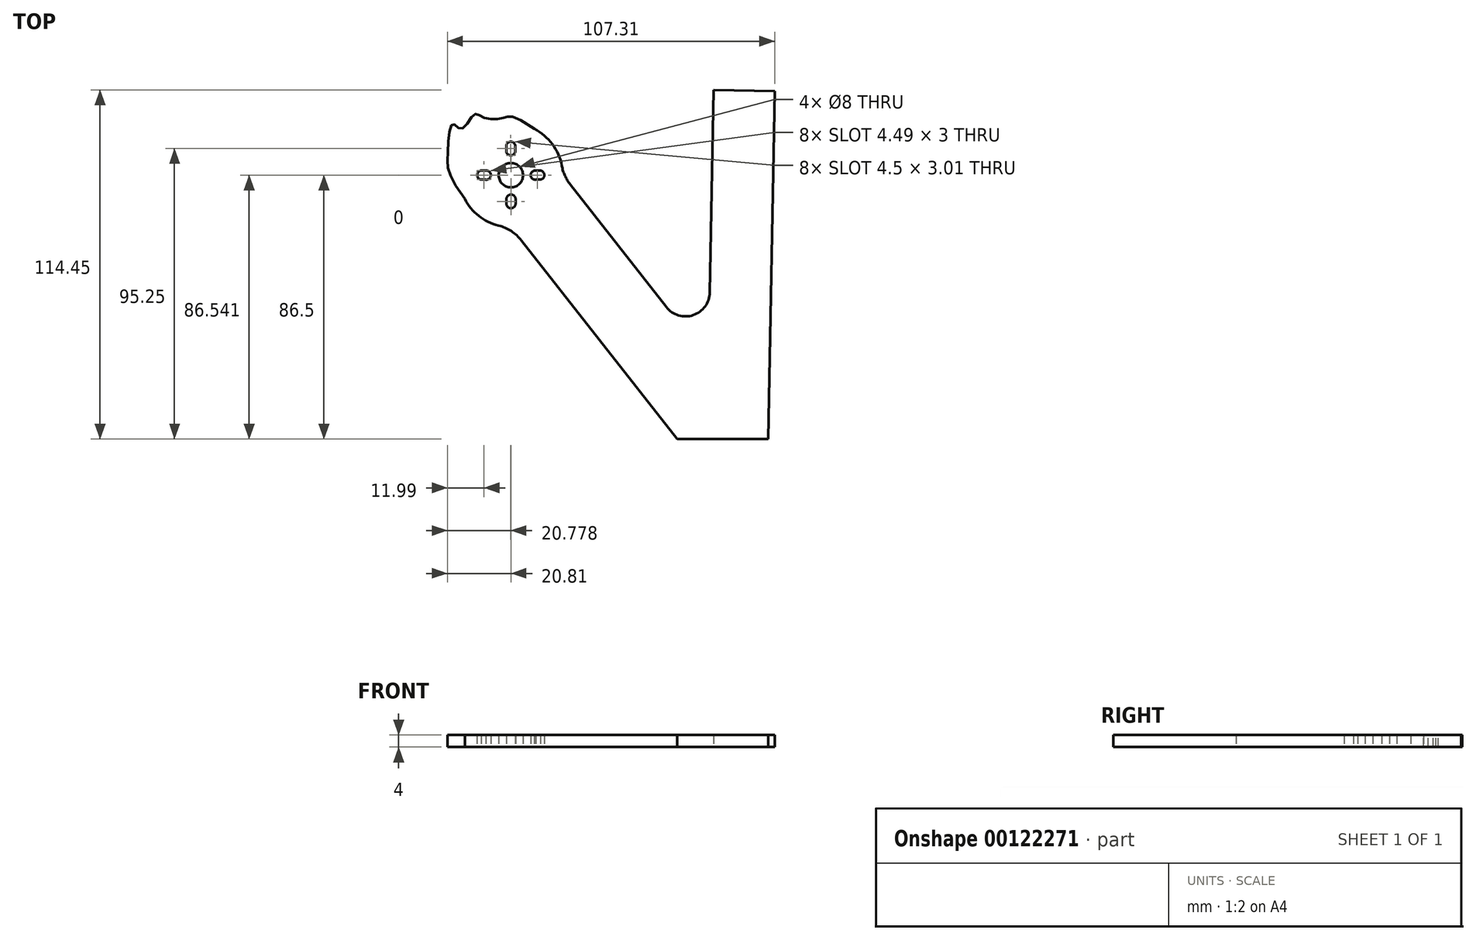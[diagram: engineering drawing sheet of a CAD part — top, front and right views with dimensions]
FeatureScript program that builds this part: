
annotation { "Feature Type Name" : "Feature", "Feature Type Description" : "" }
export const myFeature = defineFeature(function(context is Context, id is Id, definition is map)
    precondition{}
    {
        {
            var Q0;
            Q0=qCreatedBy(makeId("Top.planeOp"),FACE);
            var sketch = newSketch(context, id + "F0", { "sketchPlane" : qUnion([Q0])});
            skLineSegment(sketch, "E0", {"start": v(-20, 114.45) * mm, "end": v(-21.25, 48.07) * mm});
            skCircle(sketch, "E1", {"center": v(-86.5, 86.5) * mm, "radius": 4 * mm});
            skArc(sketch, "E2", {"start": v(-76.8, 85.05) * mm, "mid": v(-75.5, 86.64) * mm, "end": v(-77.01, 88.04) * mm});
            skLineSegment(sketch, "E3", {"start": v(-77.01, 88.04) * mm, "end": v(-78.51, 88.03) * mm});
            skLineSegment(sketch, "E4", {"start": v(-76.8, 85.05) * mm, "end": v(-78.3, 85.04) * mm});
            skArc(sketch, "E5", {"start": v(-78.51, 88.03) * mm, "mid": v(-80, 86.43) * mm, "end": v(-78.3, 85.04) * mm});
            skLineSegment(sketch, "E6", {"start": v(-86.53, 86.65) * mm, "end": v(-86.53, 97.5) * mm, "construction": true});
            skLineSegment(sketch, "E7", {"start": v(-86.5, 86.5) * mm, "end": v(-86.46, 75.65) * mm, "construction": true});
            skLineSegment(sketch, "E8.MirrorCS", {"start": v(-96.26, 85.05) * mm, "end": v(-94.76, 85.04) * mm});
            skLineSegment(sketch, "E9.MirrorCS", {"start": v(-96.06, 88.04) * mm, "end": v(-94.56, 88.03) * mm});
            skArc(sketch, "E10.MirrorCS", {"start": v(-94.56, 88.03) * mm, "mid": v(-93.07, 86.43) * mm, "end": v(-94.76, 85.04) * mm});
            skArc(sketch, "E11.MirrorCS", {"start": v(-96.26, 85.05) * mm, "mid": v(-97.57, 86.64) * mm, "end": v(-96.06, 88.04) * mm});
            skLineSegment(sketch, "E12", {"start": v(-97.57, 86.54) * mm, "end": v(-75.5, 86.62) * mm, "construction": true});
            skLineSegment(sketch, "E13.MirrorCS", {"start": v(-87.97, 78.65) * mm, "end": v(-87.97, 77.15) * mm});
            skLineSegment(sketch, "E14.MirrorCS", {"start": v(-84.97, 78.66) * mm, "end": v(-84.97, 77.16) * mm});
            skArc(sketch, "E15.MirrorCS", {"start": v(-84.97, 77.16) * mm, "mid": v(-86.46, 75.65) * mm, "end": v(-87.97, 77.15) * mm});
            skArc(sketch, "E16.MirrorCS", {"start": v(-87.97, 78.65) * mm, "mid": v(-86.48, 80.15) * mm, "end": v(-84.97, 78.66) * mm});
            skArc(sketch, "E17.MirrorCS", {"start": v(-88.03, 94.5) * mm, "mid": v(-86.52, 93) * mm, "end": v(-85.03, 94.5) * mm});
            skLineSegment(sketch, "E18.MirrorCS", {"start": v(-85.03, 94.5) * mm, "end": v(-85.03, 96) * mm});
            skLineSegment(sketch, "E19.MirrorCS", {"start": v(-88.03, 94.5) * mm, "end": v(-88.03, 96) * mm});
            skArc(sketch, "E20.MirrorCS", {"start": v(-85.03, 96) * mm, "mid": v(-86.54, 97.5) * mm, "end": v(-88.03, 96) * mm});
            skLineSegment(sketch, "E21", {"start": v(-20, 114.45) * mm, "end": v(0, 114.07) * mm});
            skLineSegment(sketch, "E22", {"start": v(0, 114.07) * mm, "end": v(-2.16, 0) * mm});
            skLineSegment(sketch, "E23", {"start": v(-86.5, 86.5) * mm, "end": v(-98.52, 98.52) * mm, "construction": true});
            skLineSegment(sketch, "E24", {"start": v(-86.53, 97.5) * mm, "end": v(-86.53, 103.5) * mm, "construction": true});
            skLineSegment(sketch, "E25", {"start": v(-97.57, 86.54) * mm, "end": v(-103.5, 86.54) * mm, "construction": true});
            skLineSegment(sketch, "E26", {"start": v(-86.46, 75.65) * mm, "end": v(-86.46, 69.5) * mm, "construction": true});
            skLineSegment(sketch, "E27", {"start": v(-86.5, 86.5) * mm, "end": v(-74.48, 98.52) * mm, "construction": true});
            skLineSegment(sketch, "E28", {"start": v(-86.5, 86.5) * mm, "end": v(-98.52, 74.48) * mm, "construction": true});
            skPoint(sketch, "E29", {"position": v(-95.85, 75.48) * mm});
            skLineSegment(sketch, "E30", {"start": v(-90.7, 90.7) * mm, "end": v(-74.48, 74.48) * mm, "construction": true});
            skCircle(sketch, "E31", {"center": v(-86.5, 86.5) * mm, "radius": 14 * mm, "construction": true});
            skArc(sketch, "E32", {"start": v(-69.78, 89.57) * mm, "mid": v(-98.14, 98.9) * mm, "end": v(-90.61, 70) * mm});
            skLineSegment(sketch, "E33", {"start": v(-82.98, 65.05) * mm, "end": v(-32, 0) * mm});
            skLineSegment(sketch, "E34", {"start": v(-67.03, 83.46) * mm, "end": v(-35.55, 43.28) * mm});
            skLineSegment(sketch, "E35", {"start": v(-75.5, 86.62) * mm, "end": v(-69.5, 86.62) * mm, "construction": true});
            skPoint(sketch, "E36.visualSharp", {"position": v(-86.46, 69.5) * mm});
            skArc(sketch, "E36.filletArc", {"start": v(-82.98, 65.05) * mm, "mid": v(-86.38, 68.17) * mm, "end": v(-90.61, 70) * mm});
            skPoint(sketch, "E37.visualSharp", {"position": v(-69.5, 86.62) * mm});
            skArc(sketch, "E37.filletArc", {"start": v(-69.78, 89.57) * mm, "mid": v(-68.78, 86.35) * mm, "end": v(-67.03, 83.46) * mm});
            skFitSpline(sketch, "E38", {"points": [v(-98.52, 74.48) * mm, v(-107.23, 93.47) * mm, v(-105.46, 103.23) * mm, v(-102.79, 101.71) * mm, v(-98.52, 106.42) * mm, v(-95.47, 105.45) * mm, v(-89.3, 105.2) * mm, v(-74.48, 98.52) * mm], "startDerivative": vector(-119.63, 160.63) * mm, "endDerivative": vector(182.1, -135.63) * mm});
            skArc(sketch, "E39.filletArc", {"start": v(-35.55, 43.28) * mm, "mid": v(-26.71, 40.63) * mm, "end": v(-21.25, 48.07) * mm});
            skLineSegment(sketch, "E40", {"start": v(-2.16, 0) * mm, "end": v(-32, 0) * mm});
            skSolve(sketch);
        }
        {
            var Q0;
            Q0 = qSketchRegion(id + "F0", true);
            extrude(context, id + "F1", {"entities" : qUnion([Q0]), "depth" : 4 * mm});
        }
    });
